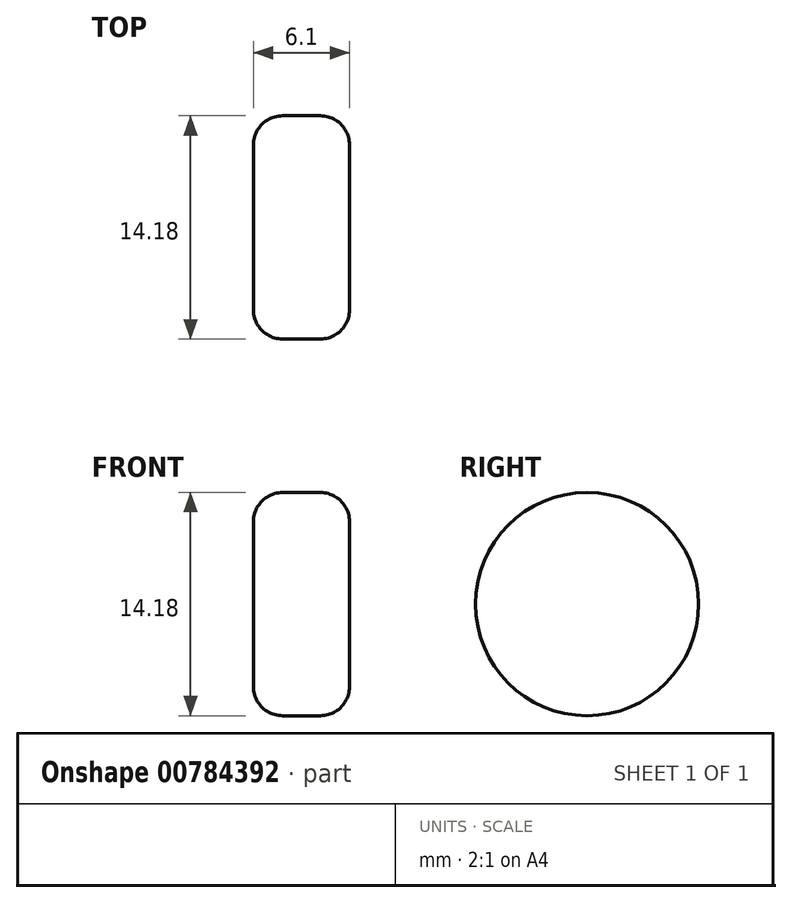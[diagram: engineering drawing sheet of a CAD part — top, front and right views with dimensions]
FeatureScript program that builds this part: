
annotation { "Feature Type Name" : "Feature", "Feature Type Description" : "" }
export const myFeature = defineFeature(function(context is Context, id is Id, definition is map)
    precondition{}
    {
        {
            var Q0;
            Q0=qCreatedBy(makeId("Right.planeOp"),FACE);
            var sketch = newSketch(context, id + "F0", { "sketchPlane" : qUnion([Q0])});
            skCircle(sketch, "E0", {"center": v(0, 0) * mm, "radius": 7.09 * mm});
            skSolve(sketch);
        }
        {
            var Q0;
            Q0=makeQuery(id+"F0.imprint","IMPRINT",FACE,{"disambiguationData":[TD([[makeQuery(id+"F0.imprint","IMPRINT",EDGE,{"derivedFrom":sQuery(id+"F0.wireOp",EDGE,"E0")}),1.0]])]});
            var Q1;
            Q1=sQuery(id+"F0.wireOp",EDGE,"E0");
            extrude(context, id + "F1", {"entities" : qUnion([Q0]), "surfaceEntities" : qUnion([Q1]), "depth" : 6.1 * mm, "offsetDistance" : 25.4 * mm});
        }
        {
            var Q0;
            Q0=makeQuery(id+"F1.opExtrude","SWEPT_FACE",FACE,{"disambiguationData":[OSD([sQuery(id+"F0.wireOp",EDGE,"E0")])]});
            fillet(context, id + "F2", {"entities" : qUnion([Q0]), "radius" : 1.84 * mm, "tangentPropagation" : true, "allowEdgeOverflow" : false});
        }
    });
